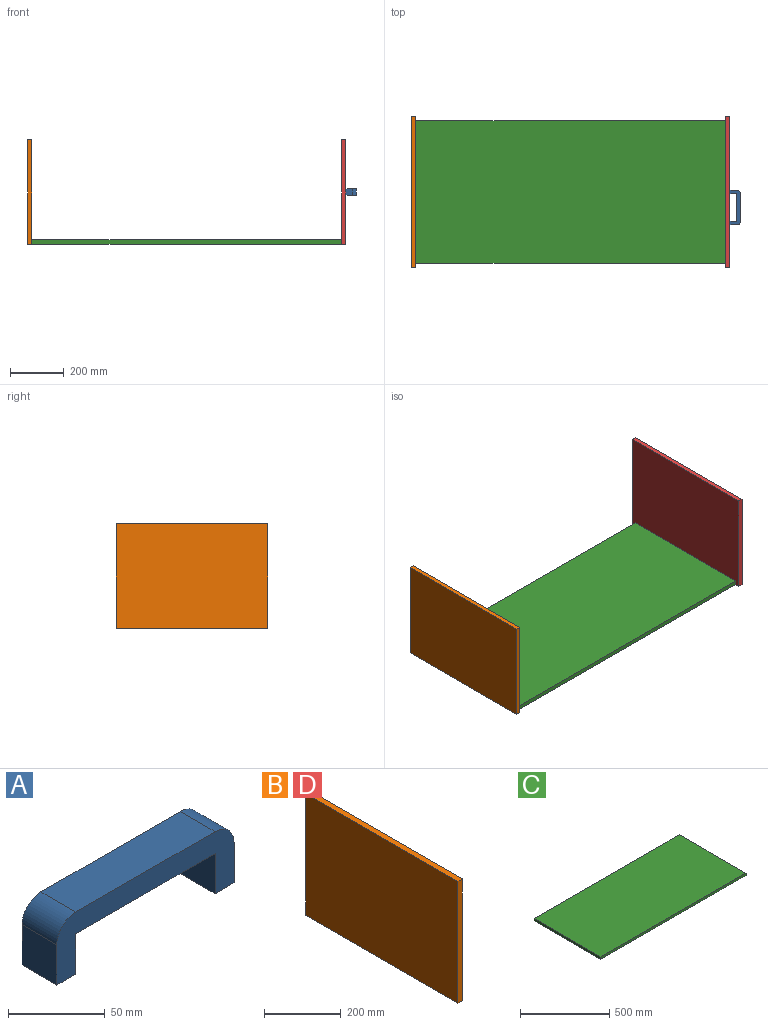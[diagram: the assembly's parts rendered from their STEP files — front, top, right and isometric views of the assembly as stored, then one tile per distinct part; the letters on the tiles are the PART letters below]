
ASSEMBLY  parts=4 mates=2
PART A: 12 faces, bbox 129.2x25.4x39.2 mm
  f0: cylinder r=13.79mm len=25.4mm, axis (0,1,0), area 550.1mm2, adj f1,f9,f10,f11
  f1: plane 25.4x25.4mm, normal (-1,0,0), area 645.2mm2, adj f0,f2,f10,f11
  f2: plane 25.4x13.79mm, normal (0,0,-1), area 350.2mm2, adj f1,f3,f10,f11
  f3: plane 25.4x25.4mm, normal (1,0,0), area 645.2mm2, adj f2,f4,f10,f11
  f4: plane 101.6x25.4mm, normal (0,0,-1), area 2580.6mm2, adj f3,f5,f10,f11
  f5: plane 25.4x25.4mm, normal (-1,0,0), area 645.2mm2, adj f4,f6,f10,f11
  f6: plane 25.4x13.79mm, normal (0,0,-1), area 350.2mm2, adj f5,f7,f10,f11
  f7: plane 25.4x25.4mm, normal (1,0,0), area 645.2mm2, adj f6,f8,f10,f11
  f8: cylinder r=13.79mm len=25.4mm, axis (0,1,0), area 550.1mm2, adj f7,f9,f10,f11
  f9: plane 101.6x25.4mm, normal (0,0,1), area 2580.6mm2, adj f0,f8,f10,f11
  f10: plane 129.18x39.19mm, normal (0,-1,0), area 2399.9mm2, adj f0,f1,f2,f3,f4,f5,f6,f7
  f11: plane 129.18x39.19mm, normal (0,1,0), area 2399.9mm2, adj f0,f1,f2,f3,f4,f5,f6,f7
PART B: 6 faces, bbox 15.9x560.4x387.4 mm
  f0: plane 560.39x15.88mm, normal (0,0,1), area 8896.2mm2, adj f1,f3,f4,f5
  f1: plane 387.35x15.88mm, normal (0,-1,0), area 6149.2mm2, adj f0,f2,f4,f5
  f2: plane 560.39x15.88mm, normal (0,0,-1), area 8896.2mm2, adj f1,f3,f4,f5
  f3: plane 387.35x15.88mm, normal (0,1,0), area 6149.2mm2, adj f0,f2,f4,f5
  f4: plane 560.39x387.35mm, normal (1,0,0), area 217066.1mm2, adj f0,f1,f2,f3
  f5: plane 560.39x387.35mm, normal (-1,0,0), area 217066.1mm2, adj f0,f1,f2,f3
PART C: 6 faces, bbox 1149.4x528.6x15.9 mm
  f0: plane 1149.35x15.88mm, normal (0,1,0), area 18245.9mm2, adj f1,f3,f4,f5
  f1: plane 528.64x15.88mm, normal (-1,0,0), area 8392.1mm2, adj f0,f2,f4,f5
  f2: plane 1149.35x15.88mm, normal (0,-1,0), area 18245.9mm2, adj f1,f3,f4,f5
  f3: plane 528.64x15.88mm, normal (1,0,0), area 8392.1mm2, adj f0,f2,f4,f5
  f4: plane 1149.35x528.64mm, normal (0,0,1), area 607589.5mm2, adj f0,f1,f2,f3
  f5: plane 1149.35x528.64mm, normal (0,0,-1), area 607589.5mm2, adj f0,f1,f2,f3
PART D: same geometry as B
PLACE A rot(axis=(0.58,0.58,0.58),120deg) t=(874.88,171.58,48.28)mm
PLACE B t=(-345.41,119.35,31.23)mm
PLACE C t=(-98.48,211.53,-158.1)mm
PLACE D t=(819.82,119.35,31.23)mm
MATE fastened C.f3 <-> D.f5  axis (1,0,0) through (819.82,219.36,-158.1)mm
MATE fastened A.f6 <-> D.f4  axis (-1,0,0) through (835.69,219.36,35.58)mm
